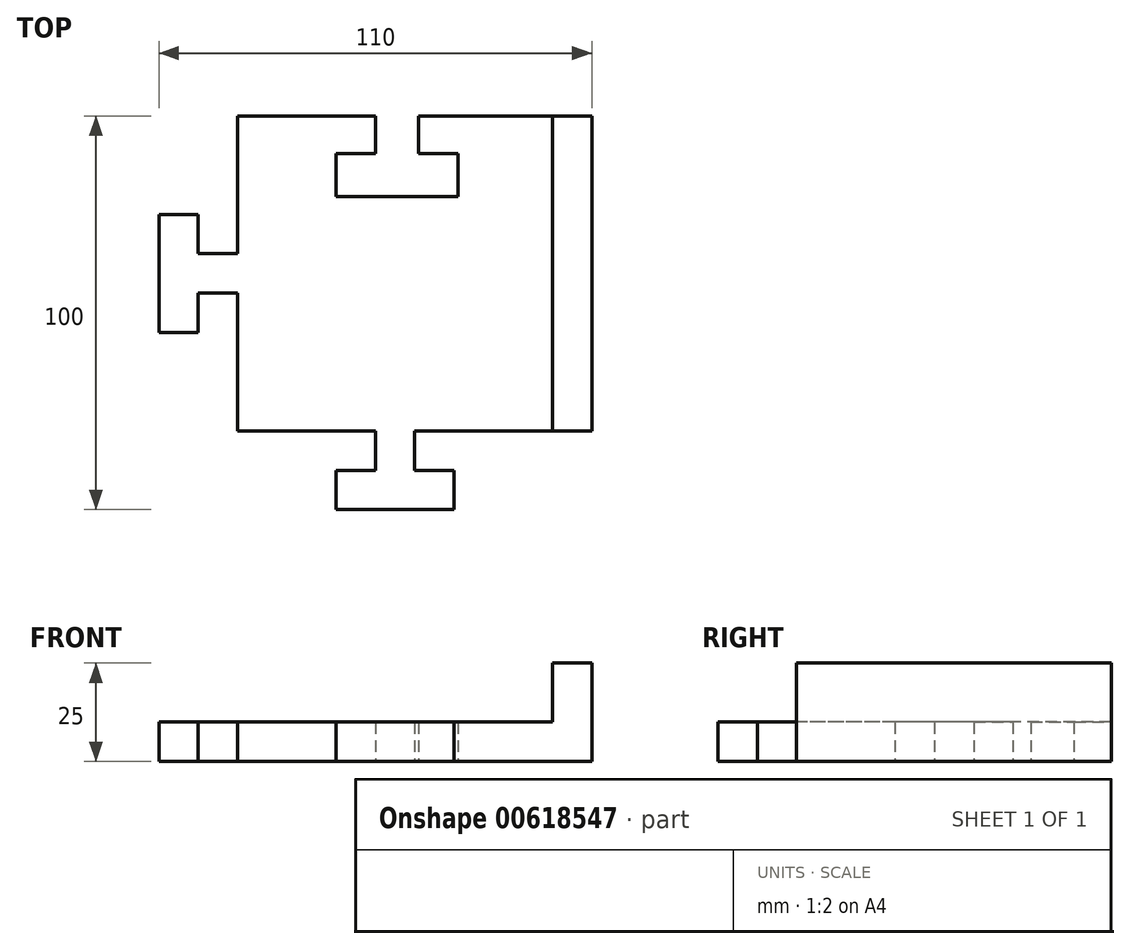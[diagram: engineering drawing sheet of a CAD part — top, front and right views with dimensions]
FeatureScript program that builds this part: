
annotation { "Feature Type Name" : "Feature", "Feature Type Description" : "" }
export const myFeature = defineFeature(function(context is Context, id is Id, definition is map)
    precondition{}
    {
        {
            var Q0;
            Q0=qCreatedBy(makeId("Top.planeOp"),FACE);
            var sketch = newSketch(context, id + "F0", { "sketchPlane" : qUnion([Q0])});
            skLineSegment(sketch, "E0.bottom", {"start": v(-40, 40) * mm, "end": v(-4.98, 40) * mm});
            skLineSegment(sketch, "E0.top", {"start": v(-40, -40) * mm, "end": v(-5, -40) * mm});
            skLineSegment(sketch, "E0.left", {"start": v(-40, 40) * mm, "end": v(-40, 5) * mm});
            skLineSegment(sketch, "E0.right", {"start": v(40, 40) * mm, "end": v(40, -40) * mm});
            skLineSegment(sketch, "E1", {"start": v(-5, -40) * mm, "end": v(-5, -50) * mm});
            skLineSegment(sketch, "E2", {"start": v(-5, -50) * mm, "end": v(-15, -50) * mm});
            skLineSegment(sketch, "E3", {"start": v(-15, -50) * mm, "end": v(-15, -60) * mm});
            skLineSegment(sketch, "E4", {"start": v(5, -50) * mm, "end": v(5, -40) * mm});
            skLineSegment(sketch, "E5", {"start": v(-15, -60) * mm, "end": v(15, -60) * mm});
            skLineSegment(sketch, "E6", {"start": v(5, -50) * mm, "end": v(15, -50) * mm});
            skLineSegment(sketch, "E7", {"start": v(15, -60) * mm, "end": v(15, -50) * mm});
            skLineSegment(sketch, "E8.trimOffspring", {"start": v(5, -40) * mm, "end": v(40, -40) * mm});
            skLineSegment(sketch, "E9.0", {"start": v(6.02, 30.52) * mm, "end": v(6.02, 40) * mm});
            skLineSegment(sketch, "E9.1", {"start": v(6.02, 30.52) * mm, "end": v(16.02, 30.52) * mm});
            skLineSegment(sketch, "E9.2", {"start": v(16.02, 19.52) * mm, "end": v(16.02, 30.52) * mm});
            skLineSegment(sketch, "E9.3", {"start": v(-4.98, 40) * mm, "end": v(-4.98, 30.52) * mm});
            skLineSegment(sketch, "E9.4", {"start": v(-4.98, 30.52) * mm, "end": v(-14.98, 30.52) * mm});
            skLineSegment(sketch, "E9.5", {"start": v(-14.98, 30.52) * mm, "end": v(-14.98, 19.52) * mm});
            skLineSegment(sketch, "E9.6", {"start": v(-14.98, 19.52) * mm, "end": v(16.02, 19.52) * mm});
            skLineSegment(sketch, "E10.trimOffspring", {"start": v(6.02, 40) * mm, "end": v(40, 40) * mm});
            skLineSegment(sketch, "E11.0", {"start": v(50, 40) * mm, "end": v(50, -40) * mm});
            skLineSegment(sketch, "E12", {"start": v(50, 40) * mm, "end": v(40, 40) * mm});
            skLineSegment(sketch, "E13", {"start": v(50, -40) * mm, "end": v(40, -40) * mm});
            skLineSegment(sketch, "E14.1.0", {"start": v(-40, 5) * mm, "end": v(-50, 5) * mm});
            skLineSegment(sketch, "E14.1.1", {"start": v(-50, -5) * mm, "end": v(-50, -15) * mm});
            skLineSegment(sketch, "E14.1.2", {"start": v(-60, -15) * mm, "end": v(-50, -15) * mm});
            skLineSegment(sketch, "E14.1.3", {"start": v(-60, 15) * mm, "end": v(-60, -15) * mm});
            skLineSegment(sketch, "E14.1.4", {"start": v(-50, 15) * mm, "end": v(-60, 15) * mm});
            skLineSegment(sketch, "E14.1.5", {"start": v(-50, 5) * mm, "end": v(-50, 15) * mm});
            skLineSegment(sketch, "E14.1.6", {"start": v(-50, -5) * mm, "end": v(-40, -5) * mm});
            skPoint(sketch, "E14.center", {"position": v(0, 0) * mm});
            skLineSegment(sketch, "E15.trimOffspring", {"start": v(-40, -5) * mm, "end": v(-40, -40) * mm});
            skSolve(sketch);
        }
        {
            var Q0;
            Q0=makeQuery(id+"F0.imprint","IMPRINT",FACE,{"disambiguationData":[TD([[makeQuery(id+"F0.imprint","IMPRINT",EDGE,{"derivedFrom":sQuery(id+"F0.wireOp",EDGE,"E0.bottom")}),-1.0]])]});
            extrude(context, id + "F1", {"entities" : qUnion([Q0]), "depth" : 10 * mm, "offsetDistance" : 25 * mm});
        }
        {
            var Q0;
            Q0=makeQuery(id+"F0.imprint","IMPRINT",FACE,{"disambiguationData":[TD([[makeQuery(id+"F0.imprint","IMPRINT",EDGE,{"derivedFrom":sQuery(id+"F0.wireOp",EDGE,"E0.right")}),1.0]])]});
            extrude(context, id + "F2", {"entities" : qUnion([Q0]), "operationType" : NewBodyOperationType.ADD, "depth" : 25 * mm, "offsetDistance" : 25 * mm});
        }
    });
